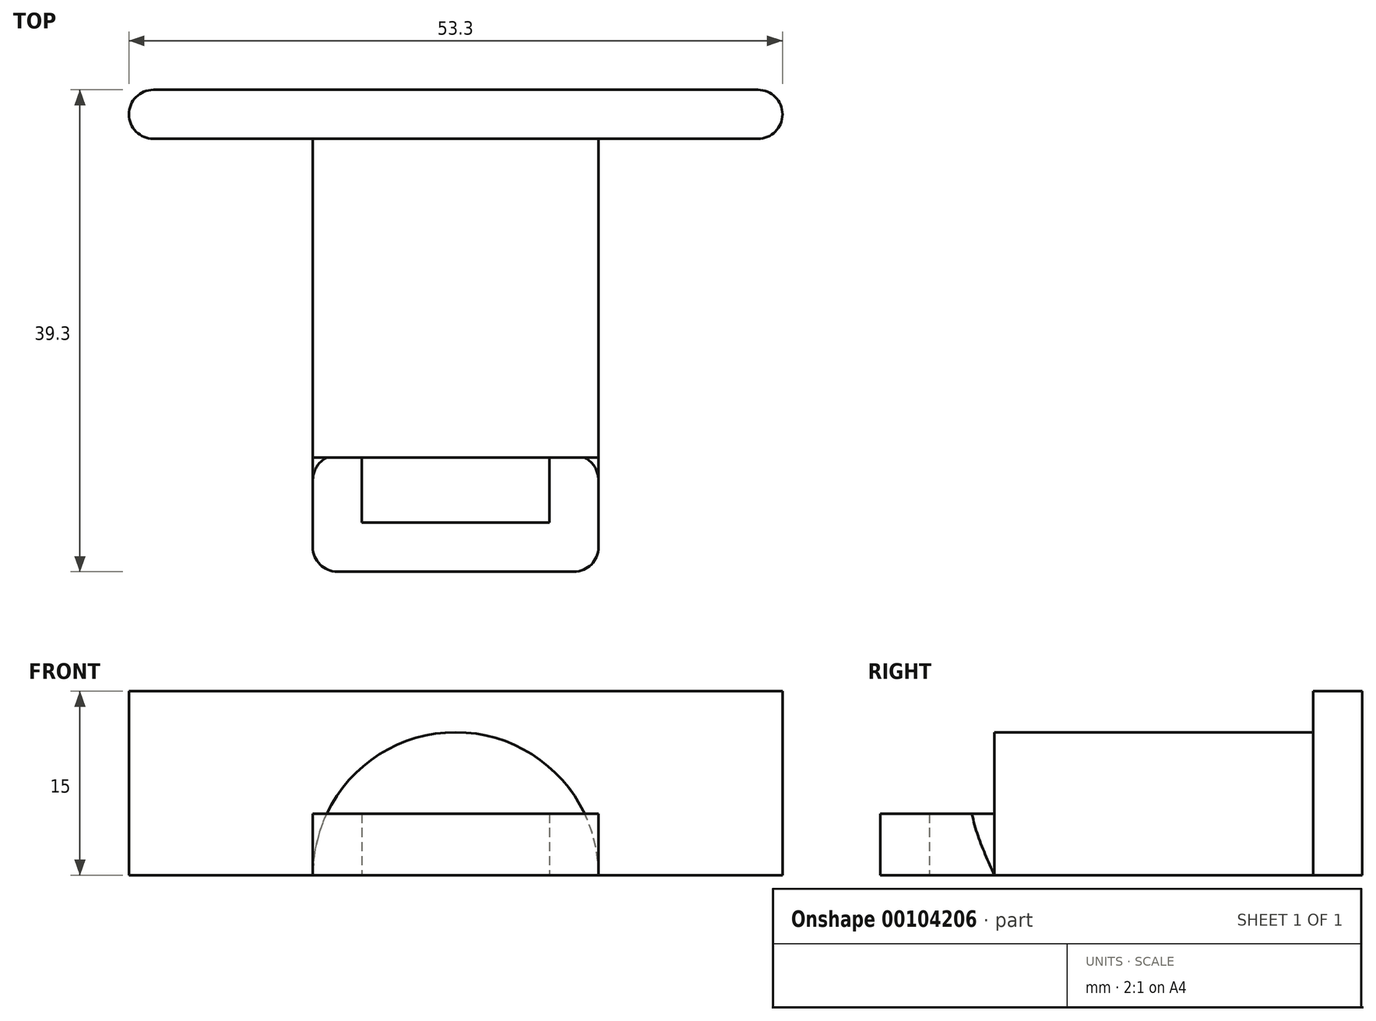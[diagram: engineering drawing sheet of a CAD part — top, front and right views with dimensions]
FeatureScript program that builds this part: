
annotation { "Feature Type Name" : "Feature", "Feature Type Description" : "" }
export const myFeature = defineFeature(function(context is Context, id is Id, definition is map)
    precondition{}
    {
        {
            var Q0;
            Q0=qCreatedBy(makeId("Top.planeOp"),FACE);
            var sketch = newSketch(context, id + "F0", { "sketchPlane" : qUnion([Q0])});
            skLineSegment(sketch, "E0.bottom", {"start": v(11.65, 19.65) * mm, "end": v(-11.65, 19.65) * mm});
            skLineSegment(sketch, "E0.top", {"start": v(11.65, -19.65) * mm, "end": v(-11.65, -19.65) * mm});
            skLineSegment(sketch, "E0.left", {"start": v(11.65, 19.65) * mm, "end": v(11.65, -19.65) * mm});
            skLineSegment(sketch, "E0.right", {"start": v(-11.65, 19.65) * mm, "end": v(-11.65, -19.65) * mm});
            skPoint(sketch, "E0.middle", {"position": v(0, 0) * mm});
            skLineSegment(sketch, "E1", {"start": v(0, -19.65) * mm, "end": v(0, 19.65) * mm});
            skLineSegment(sketch, "E2.bottom", {"start": v(-26.65, 19.65) * mm, "end": v(26.65, 19.65) * mm});
            skLineSegment(sketch, "E2.top", {"start": v(-26.65, 15.65) * mm, "end": v(26.65, 15.65) * mm});
            skLineSegment(sketch, "E2.left", {"start": v(-26.65, 19.65) * mm, "end": v(-26.65, 15.65) * mm});
            skLineSegment(sketch, "E2.right", {"start": v(26.65, 19.65) * mm, "end": v(26.65, 15.65) * mm});
            skLineSegment(sketch, "E3.bottom", {"start": v(-7.65, -15.65) * mm, "end": v(7.65, -15.65) * mm});
            skLineSegment(sketch, "E3.top", {"start": v(-7.65, -10.35) * mm, "end": v(7.65, -10.35) * mm});
            skLineSegment(sketch, "E3.left", {"start": v(-7.65, -15.65) * mm, "end": v(-7.65, -10.35) * mm});
            skLineSegment(sketch, "E3.right", {"start": v(7.65, -15.65) * mm, "end": v(7.65, -10.35) * mm});
            skLineSegment(sketch, "E4", {"start": v(-11.65, -10.35) * mm, "end": v(11.65, -10.35) * mm});
            skSolve(sketch);
        }
        {
            var Q0;
            {var subQ5=sQuery(id+"F0.wireOp",EDGE,"E2.left");Q0=makeQuery(id+"F0.imprint","IMPRINT",FACE,{"disambiguationData":[TD([[makeQuery(id+"F0.imprint","IMPRINT",EDGE,{"derivedFrom":subQ5}),1.0]])]});}
            var Q1;
            {var subQ0=sQuery(id+"F0.wireOp",EDGE,"E2.bottom");var subQ1=sQuery(id+"F0.wireOp",EDGE,"E0.right");var subQ2=makeQuery(id+"F0.imprint","INTERSECT",VERTEX,{"derivedFrom":[subQ1,subQ0]});Q1=makeQuery(id+"F0.imprint","IMPRINT",FACE,{"disambiguationData":[TD([[makeQuery(id+"F0.imprint","IMPRINT",EDGE,{"disambiguationData":[TD([[subQ2,-1.0]])],"derivedFrom":subQ1}),1.0]])]});}
            var Q2;
            {var subQ0=sQuery(id+"F0.wireOp",EDGE,"E2.bottom");var subQ1=sQuery(id+"F0.wireOp",EDGE,"E0.left");var subQ2=makeQuery(id+"F0.imprint","INTERSECT",VERTEX,{"derivedFrom":[subQ1,subQ0]});Q2=makeQuery(id+"F0.imprint","IMPRINT",FACE,{"disambiguationData":[TD([[makeQuery(id+"F0.imprint","IMPRINT",EDGE,{"disambiguationData":[TD([[subQ2,-1.0]])],"derivedFrom":subQ1}),-1.0]])]});}
            var Q3;
            {var subQ5=sQuery(id+"F0.wireOp",EDGE,"E2.right");Q3=makeQuery(id+"F0.imprint","IMPRINT",FACE,{"disambiguationData":[TD([[makeQuery(id+"F0.imprint","IMPRINT",EDGE,{"derivedFrom":subQ5}),-1.0]])]});}
            extrude(context, id + "F1", {"entities" : qUnion([Q0, Q1, Q2, Q3]), "depth" : 15 * mm});
        }
        {
            var Q0;
            {var subQ0=sQuery(id+"F0.wireOp",EDGE,"E4");var subQ6=sQuery(id+"F0.wireOp",EDGE,"E0.left");var subQ7=makeQuery(id+"F0.imprint","INTERSECT",VERTEX,{"derivedFrom":[subQ6,subQ0]});Q0=makeQuery(id+"F0.imprint","IMPRINT",FACE,{"disambiguationData":[TD([[makeQuery(id+"F0.imprint","IMPRINT",EDGE,{"disambiguationData":[TD([[subQ7,1.0]])],"derivedFrom":subQ6}),-1.0]])]});}
            var Q1;
            Q1=sQuery(id+"F0.wireOp",EDGE,"E1");
            revolve(context, id + "F2", {"operationType" : NewBodyOperationType.ADD, "entities" : qUnion([Q0]), "axis" : qUnion([Q1]), "revolveType" : RevolveType.ONE_DIRECTION, "oppositeDirection" : true, "angle" : 180 * degree});
        }
        {
            var Q0;
            {var subQ7=sQuery(id+"F0.wireOp",EDGE,"E3.left");Q0=makeQuery(id+"F0.imprint","IMPRINT",FACE,{"disambiguationData":[TD([[makeQuery(id+"F0.imprint","IMPRINT",EDGE,{"derivedFrom":subQ7}),1.0]])]});}
            var Q1;
            {var subQ9=sQuery(id+"F0.wireOp",EDGE,"E3.right");Q1=makeQuery(id+"F0.imprint","IMPRINT",FACE,{"disambiguationData":[TD([[makeQuery(id+"F0.imprint","IMPRINT",EDGE,{"derivedFrom":subQ9}),-1.0]])]});}
            extrude(context, id + "F3", {"entities" : qUnion([Q0, Q1]), "operationType" : NewBodyOperationType.ADD, "depth" : 5 * mm});
        }
        {
            var Q0;
            Q0=makeQuery(id+"F1.opExtrude","SWEPT_EDGE",EDGE,{"disambiguationData":[OSD([sQuery(id+"F0.wireOp",EDGE,"E2.top"),sQuery(id+"F0.wireOp",EDGE,"E2.left")])]});
            var Q1;
            Q1=makeQuery(id+"F1.opExtrude","SWEPT_EDGE",EDGE,{"disambiguationData":[OSD([sQuery(id+"F0.wireOp",EDGE,"E2.top"),sQuery(id+"F0.wireOp",EDGE,"E2.right")])]});
            var Q2;
            Q2=makeQuery(id+"F1.opExtrude","SWEPT_EDGE",EDGE,{"disambiguationData":[OSD([sQuery(id+"F0.wireOp",EDGE,"E2.bottom"),sQuery(id+"F0.wireOp",EDGE,"E2.left")])]});
            var Q3;
            Q3=makeQuery(id+"F1.opExtrude","SWEPT_EDGE",EDGE,{"disambiguationData":[OSD([sQuery(id+"F0.wireOp",EDGE,"E2.bottom"),sQuery(id+"F0.wireOp",EDGE,"E2.right")])]});
            var Q4;
            Q4=makeQuery(id+"F3.opExtrude","SWEPT_EDGE",EDGE,{"disambiguationData":[OSD([sQuery(id+"F0.wireOp",EDGE,"E0.top"),sQuery(id+"F0.wireOp",EDGE,"E0.left")])]});
            var Q5;
            Q5=makeQuery(id+"F3.opExtrude","SWEPT_EDGE",EDGE,{"disambiguationData":[OSD([sQuery(id+"F0.wireOp",EDGE,"E0.top"),sQuery(id+"F0.wireOp",EDGE,"E0.right")])]});
            var Q6;
            Q6=makeQuery(id+"F3.opExtrude","SWEPT_EDGE",EDGE,{"disambiguationData":[OSD([sQuery(id+"F0.wireOp",EDGE,"E0.left"),sQuery(id+"F0.wireOp",EDGE,"E4")])]});
            var Q7;
            Q7=makeQuery(id+"F3.opExtrude","SWEPT_EDGE",EDGE,{"disambiguationData":[OSD([sQuery(id+"F0.wireOp",EDGE,"E0.right"),sQuery(id+"F0.wireOp",EDGE,"E4")])]});
            fillet(context, id + "F4", {"entities" : qUnion([Q0, Q1, Q2, Q3, Q4, Q5, Q6, Q7]), "radius" : 2 * mm, "tangentPropagation" : true, "allowEdgeOverflow" : false});
        }
    });
